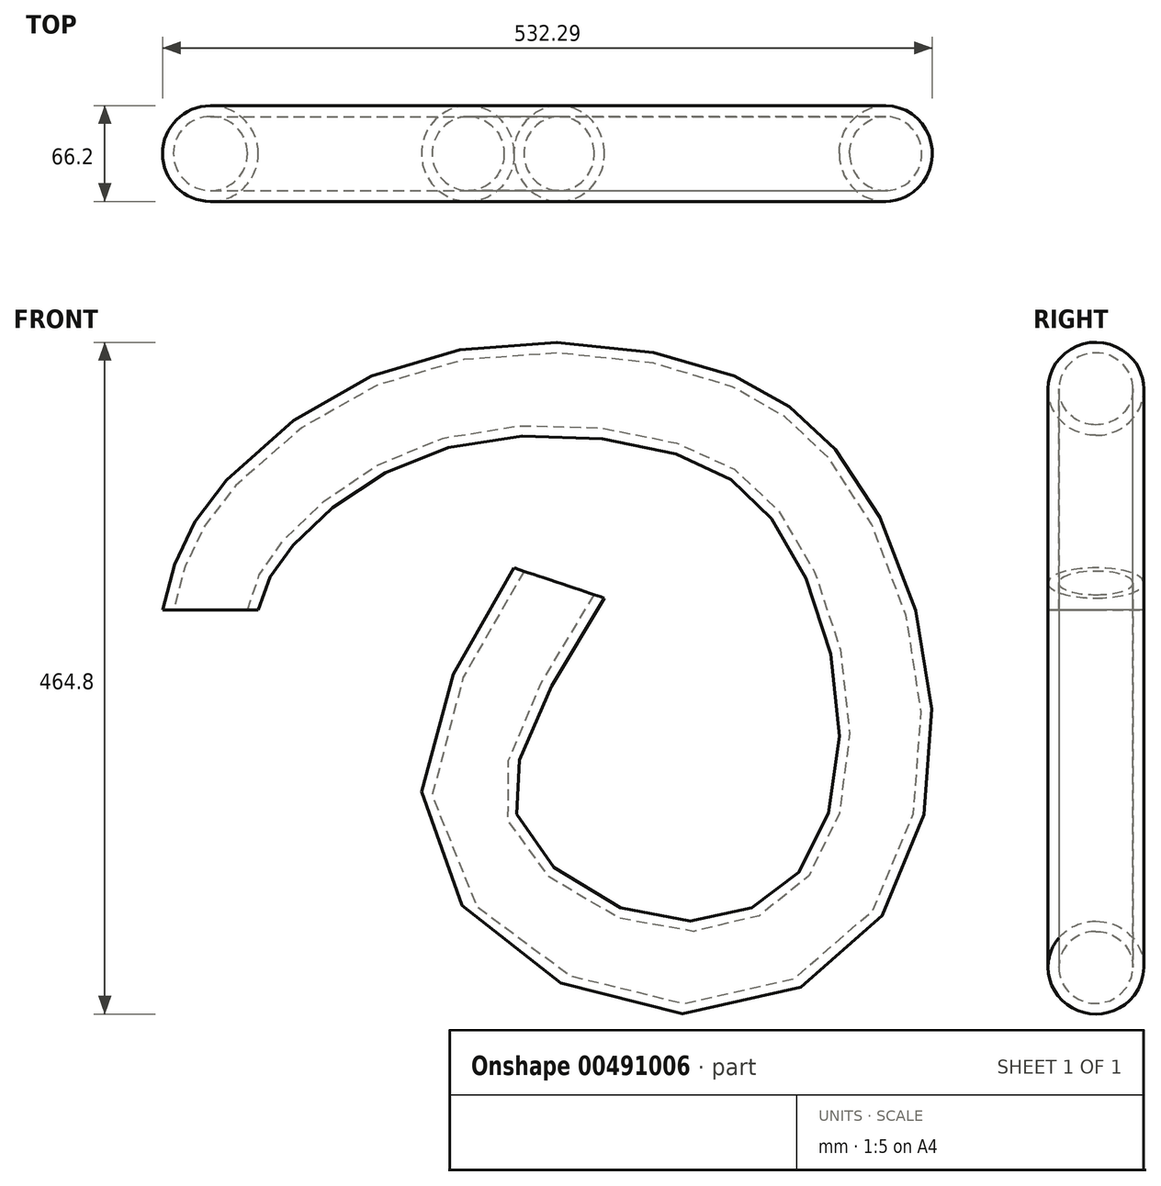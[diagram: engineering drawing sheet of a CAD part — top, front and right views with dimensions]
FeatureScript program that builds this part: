
annotation { "Feature Type Name" : "Feature", "Feature Type Description" : "" }
export const myFeature = defineFeature(function(context is Context, id is Id, definition is map)
    precondition{}
    {
        {
            var Q0;
            Q0=qCreatedBy(makeId("Top.planeOp"),FACE);
            var sketch = newSketch(context, id + "F0", { "sketchPlane" : qUnion([Q0])});
            skCircle(sketch, "E0", {"center": v(0, 0) * mm, "radius": 33.1 * mm});
            skCircle(sketch, "E1", {"center": v(0, 0) * mm, "radius": 25.62 * mm});
            skSolve(sketch);
        }
        {
            var Q0;
            Q0=qCreatedBy(makeId("Front.planeOp"),FACE);
            var sketch = newSketch(context, id + "F1", { "sketchPlane" : qUnion([Q0])});
            skFitSpline(sketch, "E2", {"points": [v(0, 0) * mm, v(12.72, 37.31) * mm, v(61.52, 93.61) * mm, v(168.58, 146.57) * mm, v(320.54, 141.96) * mm, v(410.34, 86.7) * mm, v(465.6, -58.35) * mm, v(429.91, -203.4) * mm, v(304.43, -244.85) * mm, v(181.25, -149.3) * mm, v(241.1, 18.78) * mm], "startDerivative": vector(152.64, 638.34) * mm, "endDerivative": vector(911.2, 1462.6) * mm});
            skSolve(sketch);
        }
        {
            var Q0;
            Q0=makeQuery(id+"F0.imprint","IMPRINT",FACE,{"disambiguationData":[TD([[makeQuery(id+"F0.imprint","IMPRINT",EDGE,{"derivedFrom":sQuery(id+"F0.wireOp",EDGE,"E0")}),1.0]])]});
            var Q1;
            Q1=sQuery(id+"F1.wireOp",EDGE,"E2");
            sweep(context, id + "F2", {"profiles" : qUnion([Q0]), "path" : qUnion([Q1])});
        }
    });
